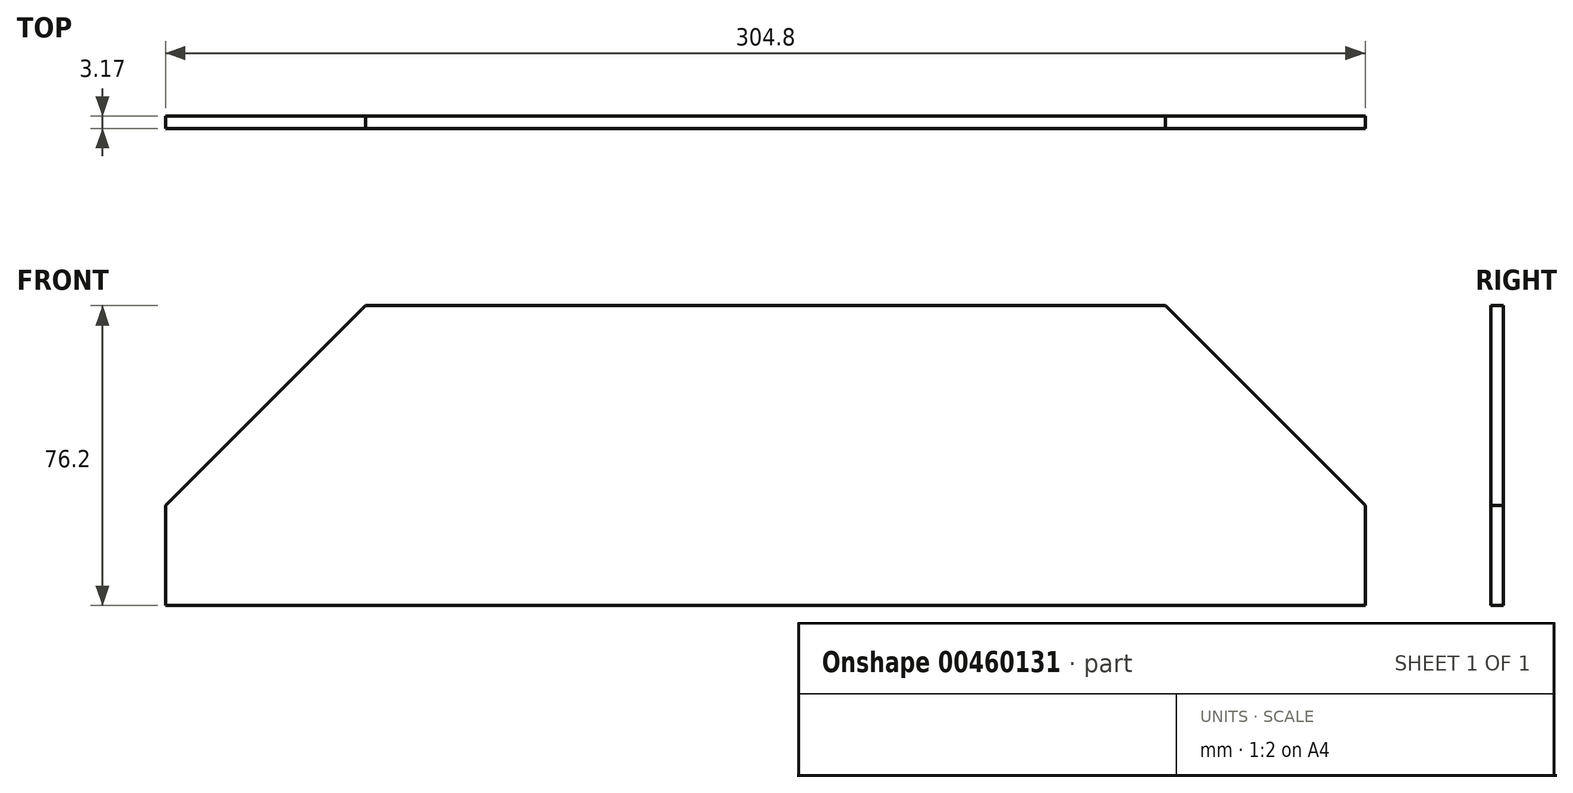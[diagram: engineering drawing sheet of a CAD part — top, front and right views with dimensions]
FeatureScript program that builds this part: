
annotation { "Feature Type Name" : "Feature", "Feature Type Description" : "" }
export const myFeature = defineFeature(function(context is Context, id is Id, definition is map)
    precondition{}
    {
        {
            var Q0;
            Q0=qCreatedBy(makeId("Front.planeOp"),FACE);
            var sketch = newSketch(context, id + "F0", { "sketchPlane" : qUnion([Q0])});
            skLineSegment(sketch, "E0", {"start": v(304.8, 0) * mm, "end": v(254, 50.8) * mm});
            skLineSegment(sketch, "E1", {"start": v(254, 50.8) * mm, "end": v(50.8, 50.8) * mm});
            skLineSegment(sketch, "E2", {"start": v(50.8, 50.8) * mm, "end": v(0, 0) * mm});
            skLineSegment(sketch, "E3", {"start": v(0, 0) * mm, "end": v(0, -25.4) * mm});
            skLineSegment(sketch, "E4", {"start": v(0, -25.4) * mm, "end": v(304.8, -25.4) * mm});
            skLineSegment(sketch, "E5", {"start": v(304.8, 0) * mm, "end": v(304.8, -25.4) * mm});
            skLineSegment(sketch, "E6", {"start": v(177.72, 0) * mm, "end": v(304.8, 0) * mm, "construction": true});
            skSolve(sketch);
        }
        {
            var Q0;
            Q0=makeQuery(id+"F0.imprint","IMPRINT",FACE,{"disambiguationData":[TD([[makeQuery(id+"F0.imprint","IMPRINT",EDGE,{"derivedFrom":sQuery(id+"F0.wireOp",EDGE,"c1m3wfPN-id9H-nvOf-0iVX-BJ8Cn2bNzFkE")}),1.0]])]});
            var Q1;
            Q1=makeQuery(id+"F0.imprint","IMPRINT",FACE,{"disambiguationData":[TD([[makeQuery(id+"F0.imprint","IMPRINT",EDGE,{"derivedFrom":sQuery(id+"F0.wireOp",EDGE,"E0")}),1.0]])]});
            extrude(context, id + "F1", {"entities" : qUnion([Q0, Q1]), "depth" : 3.17 * mm});
        }
    });
